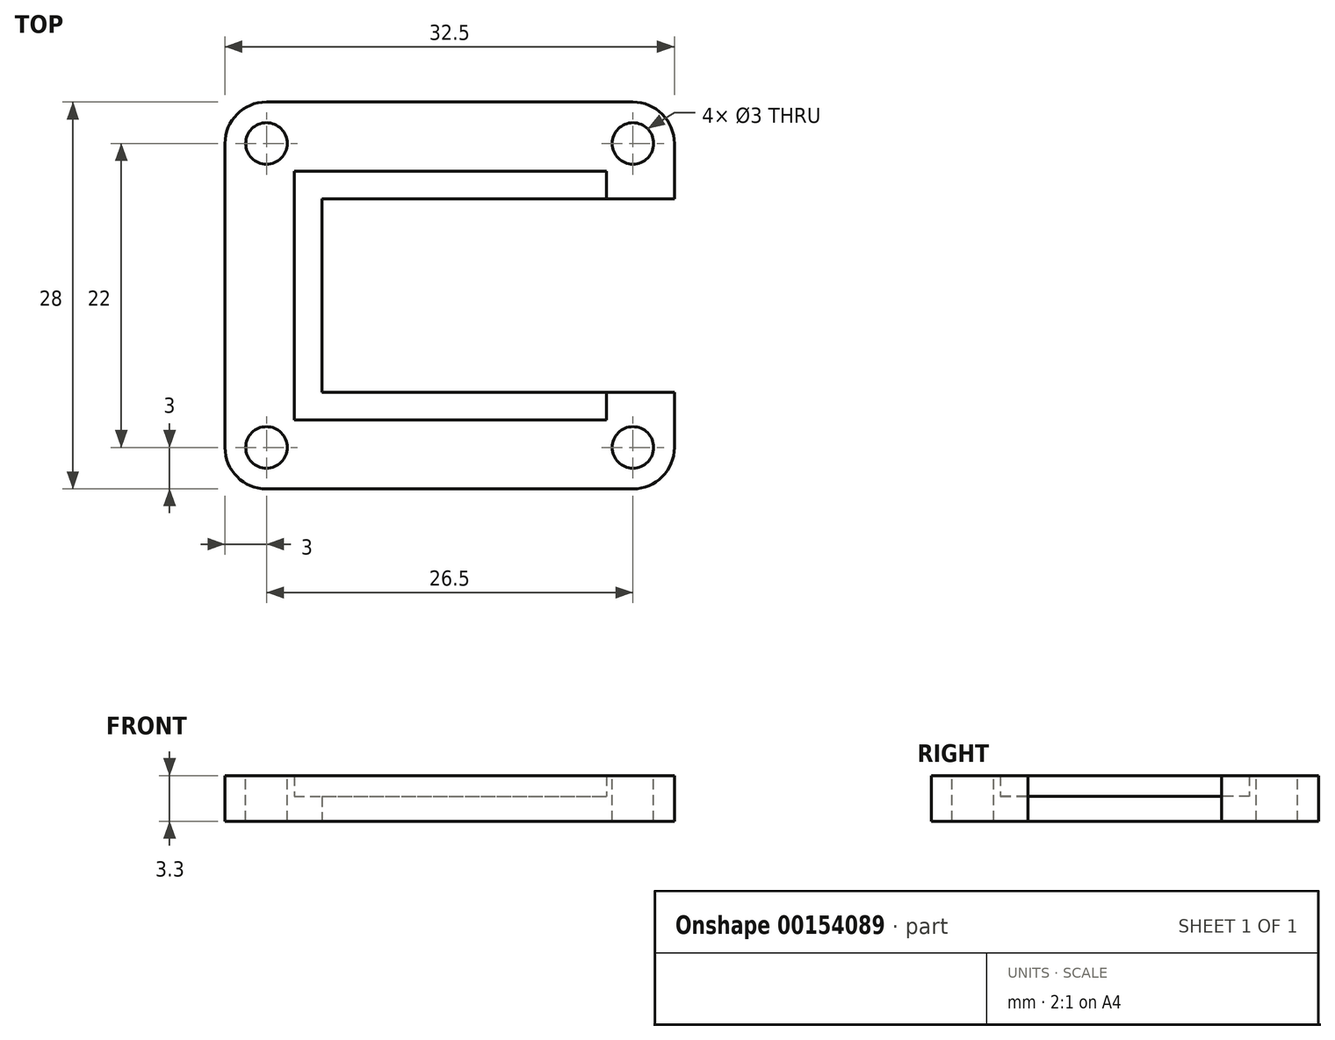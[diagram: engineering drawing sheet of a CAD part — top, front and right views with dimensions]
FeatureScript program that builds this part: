
annotation { "Feature Type Name" : "Feature", "Feature Type Description" : "" }
export const myFeature = defineFeature(function(context is Context, id is Id, definition is map)
    precondition{}
    {
        {
            var Q0;
            Q0=qCreatedBy(makeId("Top.planeOp"),FACE);
            var sketch = newSketch(context, id + "F0", { "sketchPlane" : qUnion([Q0])});
            skLineSegment(sketch, "E0.bottom", {"start": v(-14, 14) * mm, "end": v(18.5, 14) * mm});
            skLineSegment(sketch, "E0.top", {"start": v(-14, -14) * mm, "end": v(18.5, -14) * mm});
            skLineSegment(sketch, "E0.left", {"start": v(-14, 14) * mm, "end": v(-14, -14) * mm});
            skLineSegment(sketch, "E1.bottom", {"start": v(-7, 7) * mm, "end": v(18.5, 7) * mm});
            skLineSegment(sketch, "E1.top", {"start": v(-7, -7) * mm, "end": v(18.5, -7) * mm});
            skLineSegment(sketch, "E1.left", {"start": v(-7, 7) * mm, "end": v(-7, -7) * mm});
            skLineSegment(sketch, "E2", {"start": v(18.5, 14) * mm, "end": v(18.5, 7) * mm});
            skLineSegment(sketch, "E3", {"start": v(18.5, -7) * mm, "end": v(18.5, -14) * mm});
            skSolve(sketch);
        }
        {
            var Q0;
            Q0=makeQuery(id+"F0.imprint","IMPRINT",FACE,{"disambiguationData":[TD([[makeQuery(id+"F0.imprint","IMPRINT",EDGE,{"derivedFrom":sQuery(id+"F0.wireOp",EDGE,"E0.bottom")}),-1.0]])]});
            extrude(context, id + "F1", {"entities" : qUnion([Q0]), "flatOperationType" : FlatOperationType.REMOVE, "offsetDistance" : 25 * mm, "depth" : 1.8 * mm, "domain" : OperationDomain.MODEL});
        }
        {
            var Q0;
            Q0=makeQuery(id+"F1.opExtrude","CAP_FACE",FACE,{"disambiguationData":[OSD([sQuery(id+"F0.wireOp",EDGE,"E0.bottom"),sQuery(id+"F0.wireOp",EDGE,"E0.top"),sQuery(id+"F0.wireOp",EDGE,"E0.left"),sQuery(id+"F0.wireOp",EDGE,"E0.right"),sQuery(id+"F0.wireOp",EDGE,"01479c32-d564-44ff-8063-f80d61345cff"),sQuery(id+"F0.wireOp",EDGE,"98e111b2-c3b8-48e0-8128-5d89a61d85a6"),sQuery(id+"F0.wireOp",EDGE,"3f0c3ad8-cc05-463a-92c9-4b5e842daafb"),sQuery(id+"F0.wireOp",EDGE,"ad23b29c-1861-4b1d-97c7-9bc15cb9d7c6"),sQuery(id+"F0.wireOp",EDGE,"E1.bottom"),sQuery(id+"F0.wireOp",EDGE,"E1.top"),sQuery(id+"F0.wireOp",EDGE,"E1.left"),sQuery(id+"F0.wireOp",EDGE,"E1.right")])],"isStart":false});
            var sketch = newSketch(context, id + "F2", { "sketchPlane" : qUnion([Q0])});
            skLineSegment(sketch, "E4.bottom", {"start": v(-9, 9) * mm, "end": v(13.6, 9) * mm});
            skLineSegment(sketch, "E4.top", {"start": v(-9, -9) * mm, "end": v(13.6, -9) * mm});
            skLineSegment(sketch, "E4.left", {"start": v(-9, 9) * mm, "end": v(-9, -9) * mm});
            skLineSegment(sketch, "E5.bottom", {"start": v(-14, 14) * mm, "end": v(-14, 14) * mm});
            skLineSegment(sketch, "E5.top", {"start": v(-14, -14) * mm, "end": v(-14, -14) * mm});
            skLineSegment(sketch, "E5.left", {"start": v(-14, 14) * mm, "end": v(-14, -14) * mm});
            skLineSegment(sketch, "E5.right", {"start": v(-14, 14) * mm, "end": v(-14, -14) * mm});
            skLineSegment(sketch, "E6", {"start": v(-14, 14) * mm, "end": v(18.5, 14) * mm});
            skLineSegment(sketch, "E7", {"start": v(18.5, -14) * mm, "end": v(-14, -14) * mm});
            skLineSegment(sketch, "E8", {"start": v(18.5, 14) * mm, "end": v(18.5, 7) * mm});
            skLineSegment(sketch, "E9", {"start": v(13.6, 9) * mm, "end": v(13.6, 7) * mm});
            skLineSegment(sketch, "E10", {"start": v(13.6, 7) * mm, "end": v(18.5, 7) * mm});
            skLineSegment(sketch, "E11", {"start": v(13.6, -9) * mm, "end": v(13.6, -7) * mm});
            skLineSegment(sketch, "E12", {"start": v(13.6, -7) * mm, "end": v(18.5, -7) * mm});
            skLineSegment(sketch, "E13", {"start": v(18.5, -7) * mm, "end": v(18.5, -14) * mm});
            skSolve(sketch);
        }
        {
            var Q0;
            Q0 = qSketchRegion(id + "F2", true);
            extrude(context, id + "F3", {"entities" : qUnion([Q0]), "operationType" : NewBodyOperationType.ADD, "flatOperationType" : FlatOperationType.REMOVE, "offsetDistance" : 25 * mm, "depth" : 1.5 * mm, "domain" : OperationDomain.MODEL});
        }
        {
            var Q0;
            Q0=makeQuery(id+"F3.opExtrude","CAP_FACE",FACE,{"disambiguationData":[OSD([sQuery(id+"F2.wireOp",EDGE,"E4.bottom"),sQuery(id+"F2.wireOp",EDGE,"E4.top"),sQuery(id+"F2.wireOp",EDGE,"E4.left"),sQuery(id+"F2.wireOp",EDGE,"E4.right"),sQuery(id+"F2.wireOp",EDGE,"E5.right"),sQuery(id+"F2.wireOp",EDGE,"E6"),sQuery(id+"F2.wireOp",EDGE,"VorFtXou-mvhi-hjxP-X2bf-h0GdYhb3dMXb"),sQuery(id+"F2.wireOp",EDGE,"E7")])],"isStart":false});
            var sketch = newSketch(context, id + "F4", { "sketchPlane" : qUnion([Q0])});
            skCircle(sketch, "E14", {"center": v(-11, 11) * mm, "radius": 1.5 * mm});
            skCircle(sketch, "E15", {"center": v(15.5, 11) * mm, "radius": 1.5 * mm});
            skCircle(sketch, "E16", {"center": v(15.5, -11) * mm, "radius": 1.5 * mm});
            skCircle(sketch, "E17", {"center": v(-11, -11) * mm, "radius": 1.5 * mm});
            skSolve(sketch);
        }
        {
            var Q0;
            Q0 = qSketchRegion(id + "F4", true);
            extrude(context, id + "F5", {"entities" : qUnion([Q0]), "operationType" : NewBodyOperationType.REMOVE, "endBound" : BoundingType.UP_TO_NEXT, "oppositeDirection" : true, "depth" : 25 * mm});
        }
        {
            var Q0;
            Q0=makeQuery(id+"F3.boolean.opBoolean","MERGE",EDGE,{"derivedFrom":[makeQuery(id+"F1.opExtrude","SWEPT_EDGE",EDGE,{"disambiguationData":[OSD([sQuery(id+"F0.wireOp",EDGE,"E0.top"),sQuery(id+"F0.wireOp",EDGE,"E0.left")])]}),makeQuery(id+"F3.opExtrude","SWEPT_EDGE",EDGE,{"disambiguationData":[OSD([sQuery(id+"F2.wireOp",EDGE,"E5.right"),sQuery(id+"F2.wireOp",EDGE,"E7")])]})]});
            var Q1;
            Q1=makeQuery(id+"F3.boolean.opBoolean","MERGE",EDGE,{"derivedFrom":[makeQuery(id+"F1.opExtrude","SWEPT_EDGE",EDGE,{"disambiguationData":[OSD([sQuery(id+"F0.wireOp",EDGE,"E0.top"),sQuery(id+"F0.wireOp",EDGE,"E3")])]}),makeQuery(id+"F3.opExtrude","SWEPT_EDGE",EDGE,{"disambiguationData":[OSD([sQuery(id+"F2.wireOp",EDGE,"VorFtXou-mvhi-hjxP-X2bf-h0GdYhb3dMXb"),sQuery(id+"F2.wireOp",EDGE,"E7")])]})]});
            var Q2;
            Q2=makeQuery(id+"F3.boolean.opBoolean","MERGE",EDGE,{"derivedFrom":[makeQuery(id+"F1.opExtrude","SWEPT_EDGE",EDGE,{"disambiguationData":[OSD([sQuery(id+"F0.wireOp",EDGE,"E0.bottom"),sQuery(id+"F0.wireOp",EDGE,"E2")])]}),makeQuery(id+"F3.opExtrude","SWEPT_EDGE",EDGE,{"disambiguationData":[OSD([sQuery(id+"F2.wireOp",EDGE,"E6"),sQuery(id+"F2.wireOp",EDGE,"VorFtXou-mvhi-hjxP-X2bf-h0GdYhb3dMXb")])]})]});
            var Q3;
            Q3=makeQuery(id+"F3.boolean.opBoolean","MERGE",EDGE,{"derivedFrom":[makeQuery(id+"F1.opExtrude","SWEPT_EDGE",EDGE,{"disambiguationData":[OSD([sQuery(id+"F0.wireOp",EDGE,"E0.bottom"),sQuery(id+"F0.wireOp",EDGE,"E0.left")])]}),makeQuery(id+"F3.opExtrude","SWEPT_EDGE",EDGE,{"disambiguationData":[OSD([sQuery(id+"F2.wireOp",EDGE,"E5.right"),sQuery(id+"F2.wireOp",EDGE,"E6")])]})]});
            fillet(context, id + "F6", {"entities" : qUnion([Q0, Q1, Q2, Q3]), "radius" : 3 * mm, "tangentPropagation" : true, "allowEdgeOverflow" : false});
        }
    });
